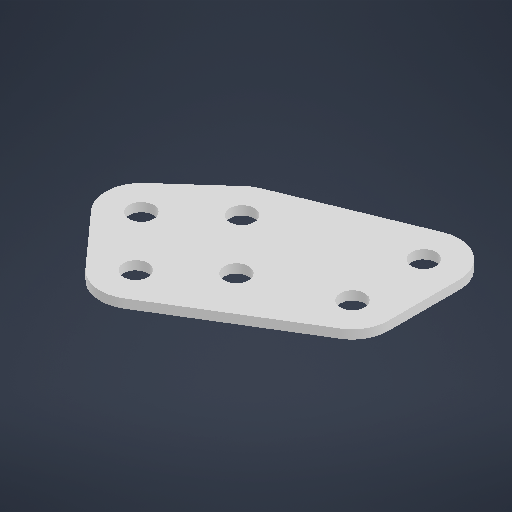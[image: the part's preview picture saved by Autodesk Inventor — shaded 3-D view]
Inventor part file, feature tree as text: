
AUTODESK INVENTOR PART (.ipt)
format: ipt  version: 2025.2 (Build 292293000, 293)  size: 206,848 bytes
history: native  units: in
note: dims shown in document units (in); Inventor stores cm internally (conversion verified against a paired STEP export)
features: extrude x1, sketch x1
ambient origin geometry x8: Origin, YZ Plane, XZ Plane, XY Plane, X Axis, Y Axis, Z Axis, Center Point
bodies: Solid1 (feature_tree)
feature tree (2):
  extrude  "Extrusion1"  Depth=0.0625in TaperAngle=0.0deg
  sketch  "Sketch1"  dims[d0=0.5in d1=0.5in d2=0.5in d3=0.5in d4=0.5in d5=0.5in d7=0.0625in d8=0.0in]
